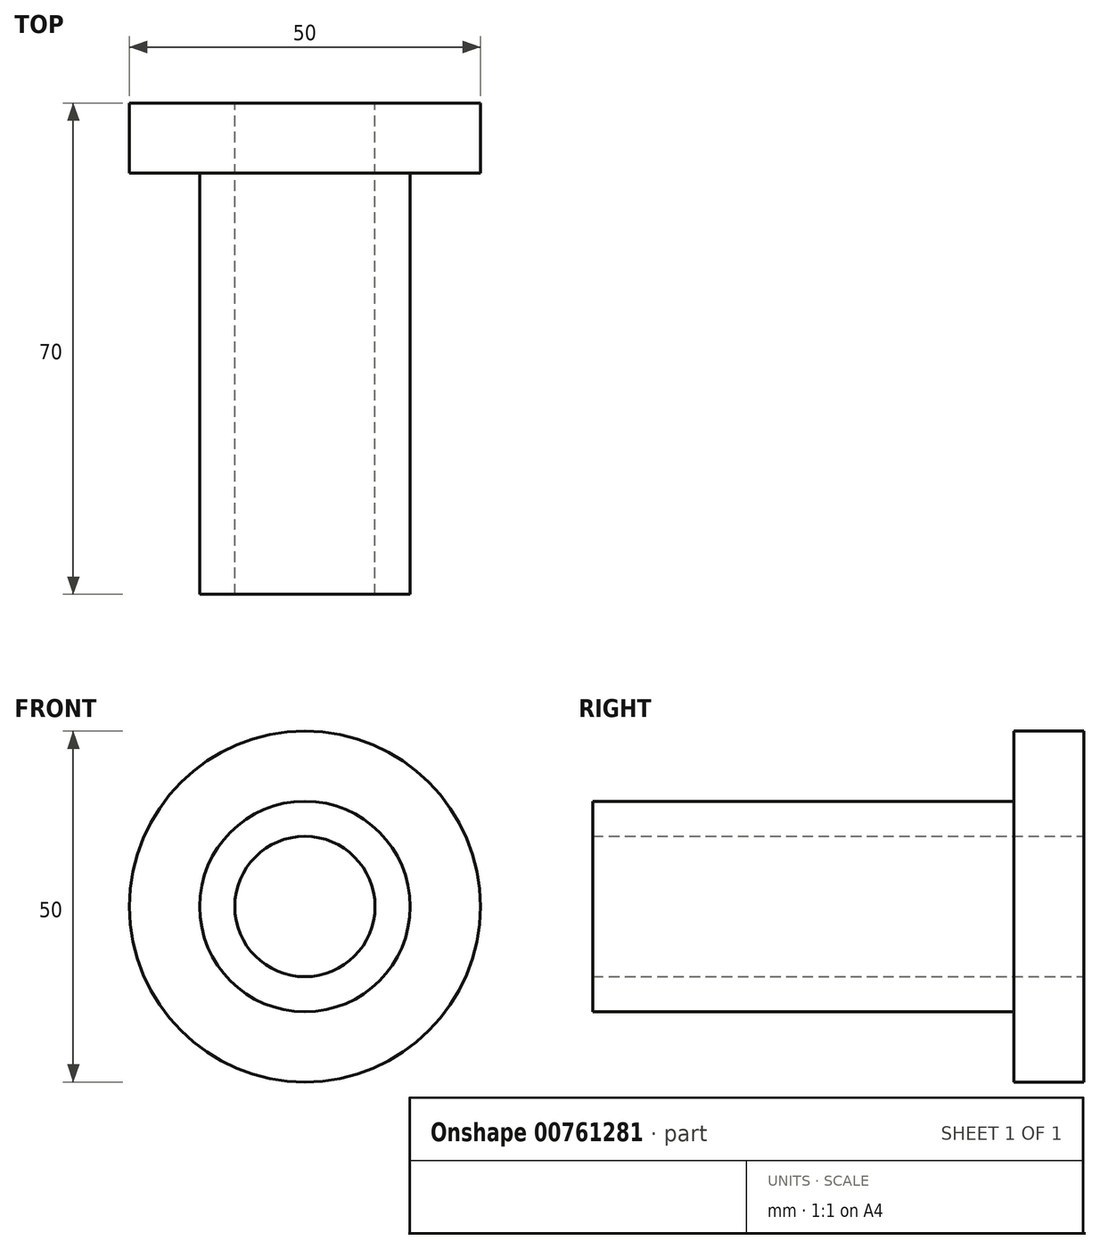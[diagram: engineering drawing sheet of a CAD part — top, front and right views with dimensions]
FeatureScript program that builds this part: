
annotation { "Feature Type Name" : "Feature", "Feature Type Description" : "" }
export const myFeature = defineFeature(function(context is Context, id is Id, definition is map)
    precondition{}
    {
        {
            var Q0;
            Q0=qCreatedBy(makeId("Front.planeOp"),FACE);
            var sketch = newSketch(context, id + "F0", { "sketchPlane" : qUnion([Q0])});
            skCircle(sketch, "E0", {"center": v(0, 0) * mm, "radius": 25 * mm});
            skCircle(sketch, "E1", {"center": v(0, 0) * mm, "radius": 10 * mm});
            skCircle(sketch, "E2", {"center": v(0, 0) * mm, "radius": 15 * mm});
            skSolve(sketch);
        }
        {
            var Q0;
            Q0=makeQuery(id+"F0.imprint","IMPRINT",FACE,{"disambiguationData":[TD([[makeQuery(id+"F0.imprint","IMPRINT",EDGE,{"derivedFrom":sQuery(id+"F0.wireOp",EDGE,"E0")}),1.0]])]});
            var sketch = newSketch(context, id + "F1", { "sketchPlane" : qUnion([Q0])});
            skSolve(sketch);
        }
        {
            var Q0;
            Q0=makeQuery(id+"F1.imprint","IMPRINT",FACE,{"disambiguationData":[TD([[makeQuery(id+"F1.imprint","IMPRINT",EDGE,{"derivedFrom":makeQuery(id+"F0.imprint","IMPRINT",EDGE,{"derivedFrom":sQuery(id+"F0.wireOp",EDGE,"E0")})}),1.0]])]});
            extrude(context, id + "F2", {"entities" : qUnion([Q0]), "depth" : 10 * mm, "offsetDistance" : 25 * mm});
        }
        {
            var Q0;
            Q0=makeQuery(id+"F0.imprint","IMPRINT",FACE,{"disambiguationData":[TD([[makeQuery(id+"F0.imprint","IMPRINT",EDGE,{"derivedFrom":sQuery(id+"F0.wireOp",EDGE,"E1")}),-1.0]])]});
            extrude(context, id + "F3", {"entities" : qUnion([Q0]), "operationType" : NewBodyOperationType.ADD, "depth" : 70 * mm, "offsetDistance" : 25 * mm});
        }
    });
